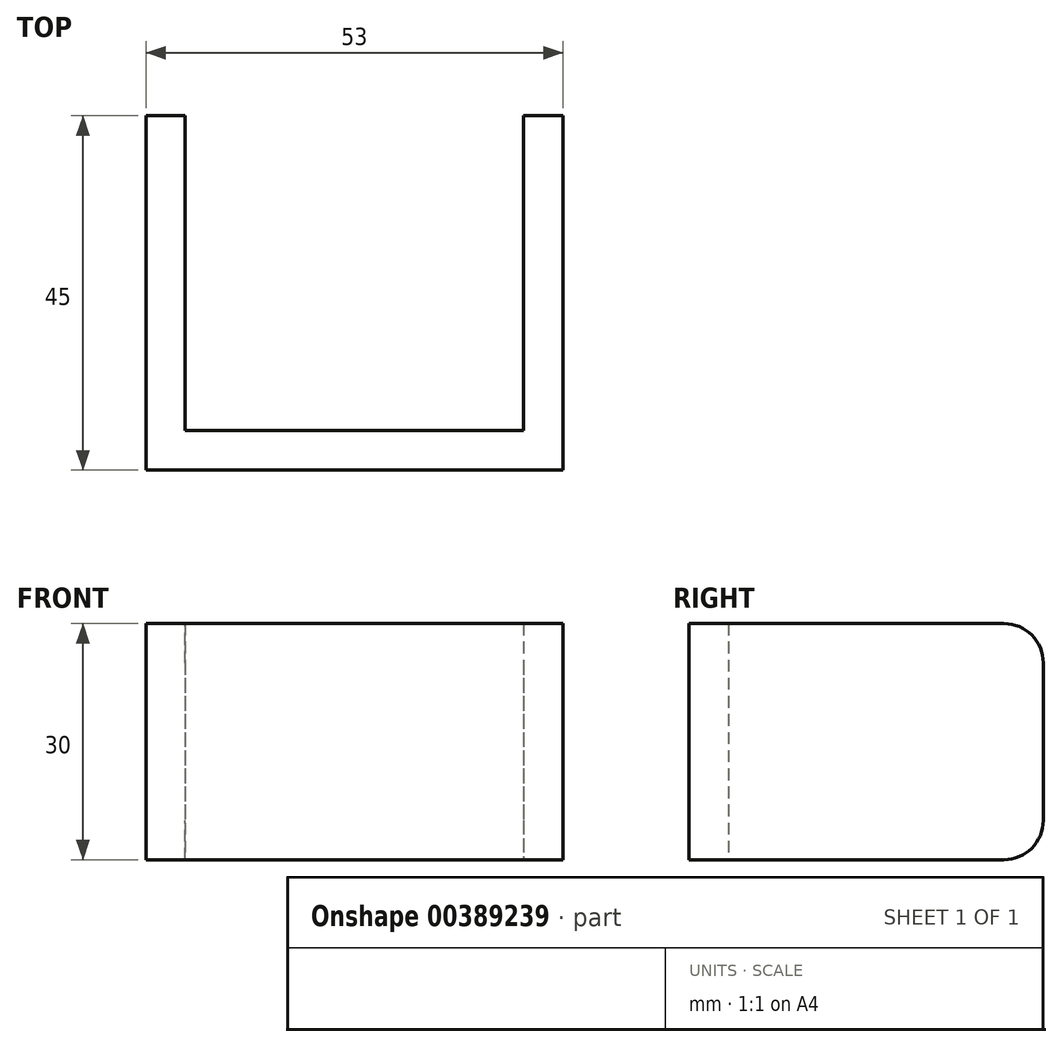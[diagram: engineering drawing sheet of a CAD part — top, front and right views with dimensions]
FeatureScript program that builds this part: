
annotation { "Feature Type Name" : "Feature", "Feature Type Description" : "" }
export const myFeature = defineFeature(function(context is Context, id is Id, definition is map)
    precondition{}
    {
        {
            var Q0;
            Q0=qCreatedBy(makeId("Top.planeOp"),FACE);
            var sketch = newSketch(context, id + "F0", { "sketchPlane" : qUnion([Q0])});
            skLineSegment(sketch, "E0", {"start": v(0, 0) * mm, "end": v(-53, 0) * mm});
            skLineSegment(sketch, "E1", {"start": v(-53, 0) * mm, "end": v(-53, 45) * mm});
            skLineSegment(sketch, "E2", {"start": v(-53, 45) * mm, "end": v(-48, 45) * mm});
            skLineSegment(sketch, "E3", {"start": v(-48, 45) * mm, "end": v(-48, 5) * mm});
            skLineSegment(sketch, "E4", {"start": v(-48, 5) * mm, "end": v(-5, 5) * mm});
            skLineSegment(sketch, "E5", {"start": v(-5, 5) * mm, "end": v(-5, 45) * mm});
            skPoint(sketch, "E5.endSnap0", {"position": v(-50.5, 45) * mm});
            skLineSegment(sketch, "E6", {"start": v(-5, 45) * mm, "end": v(0, 45) * mm});
            skLineSegment(sketch, "E7", {"start": v(0, 45) * mm, "end": v(0, 0) * mm});
            skSolve(sketch);
        }
        {
            var Q0;
            Q0 = qSketchRegion(id + "F0", true);
            extrude(context, id + "F1", {"entities" : qUnion([Q0]), "depth" : 30 * mm});
        }
        {
            var Q0;
            Q0=makeQuery(id+"F1.opExtrude","CAP_EDGE",EDGE,{"disambiguationData":[OSD([sQuery(id+"F0.wireOp",EDGE,"E2")])],"isStart":false});
            var Q1;
            Q1=makeQuery(id+"F1.opExtrude","CAP_EDGE",EDGE,{"disambiguationData":[OSD([sQuery(id+"F0.wireOp",EDGE,"E6")])],"isStart":false});
            var Q2;
            Q2=makeQuery(id+"F1.opExtrude","CAP_EDGE",EDGE,{"disambiguationData":[OSD([sQuery(id+"F0.wireOp",EDGE,"E6")])],"isStart":true});
            var Q3;
            Q3=makeQuery(id+"F1.opExtrude","CAP_EDGE",EDGE,{"disambiguationData":[OSD([sQuery(id+"F0.wireOp",EDGE,"E2")])],"isStart":true});
            fillet(context, id + "F2", {"entities" : qUnion([Q0, Q1, Q2, Q3]), "radius" : 5 * mm, "tangentPropagation" : true, "allowEdgeOverflow" : false});
        }
    });
